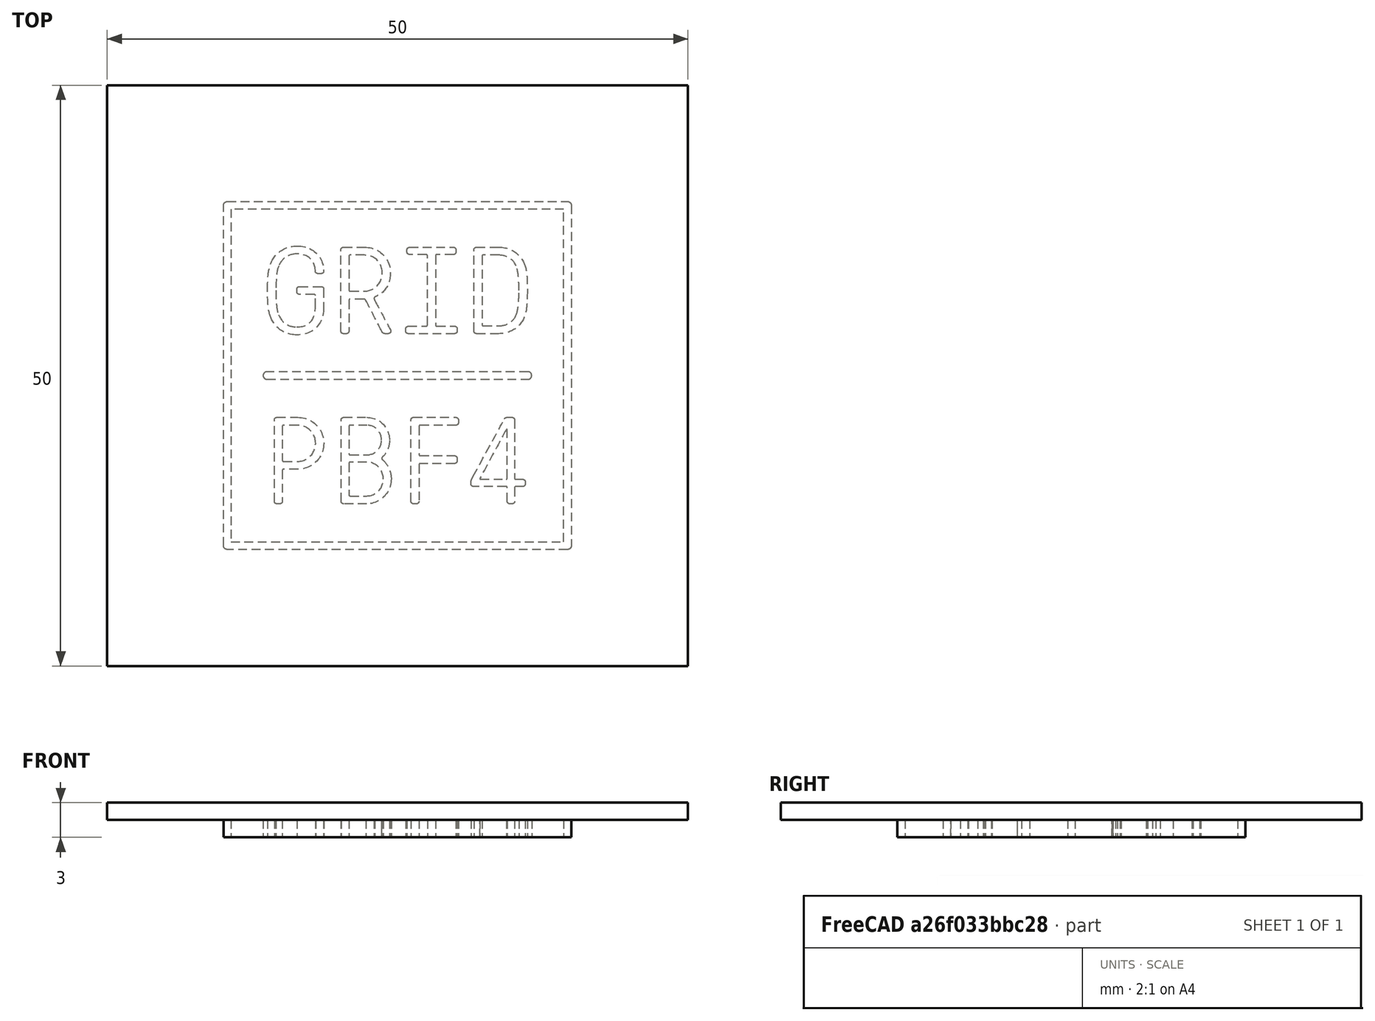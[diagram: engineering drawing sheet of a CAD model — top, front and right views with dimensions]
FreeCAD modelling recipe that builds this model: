
FCSTD DOCUMENT  (FreeCAD 0.18R16131 (Git))
Label: Pbf4 Logo 5cm
License: All rights reserved
LicenseURL: http://en.wikipedia.org/wiki/All_rights_reserved
objects: Sketcher::SketchObject×3, PartDesign::Pad×3, PartDesign::Body×1
note: 10 computed .brp shape members not serialized (recipe doc carries the construction recipe); baked Part::Feature solids carry a one-line shape summary decoded from their .brp

FEATURE [Sketcher::SketchObject] Sketch017
  sketch-geometry (12):
    g0: BSplineCurve PolesCount=2 KnotsCount=2 Degree=1 IsPeriodic=0
    g1: BSplineCurve PolesCount=2 KnotsCount=2 Degree=1 IsPeriodic=0
    g2: BSplineCurve PolesCount=2 KnotsCount=2 Degree=1 IsPeriodic=0
    g3: BSplineCurve PolesCount=2 KnotsCount=2 Degree=1 IsPeriodic=0
    g4: BSplineCurve PolesCount=2 KnotsCount=2 Degree=1 IsPeriodic=0
    g5: BSplineCurve PolesCount=4 KnotsCount=2 Degree=3 IsPeriodic=0
    g6: BSplineCurve PolesCount=2 KnotsCount=2 Degree=1 IsPeriodic=0
    g7: BSplineCurve PolesCount=4 KnotsCount=2 Degree=3 IsPeriodic=0
    g8: BSplineCurve PolesCount=2 KnotsCount=2 Degree=1 IsPeriodic=0
    g9: BSplineCurve PolesCount=4 KnotsCount=2 Degree=3 IsPeriodic=0
    g10: BSplineCurve PolesCount=2 KnotsCount=2 Degree=1 IsPeriodic=0
    g11: BSplineCurve PolesCount=4 KnotsCount=2 Degree=3 IsPeriodic=0
  constraints (12):
    c: Coincident(g0,g1)
    c: Coincident(g1,g2)
    c: Coincident(g2,g3)
    c: Coincident(g3,g0)
    c: Coincident(g4,g5)
    c: Coincident(g5,g6)
    c: Coincident(g6,g7)
    c: Coincident(g7,g8)
    c: Coincident(g8,g9)
    c: Coincident(g9,g10)
    c: Coincident(g10,g11)
    c: Coincident(g11,g4)
FEATURE [Sketcher::SketchObject] Sketch018
  sketch-geometry (189):
    g0: BSplineCurve PolesCount=4 KnotsCount=2 Degree=3 IsPeriodic=0
    g1: BSplineCurve PolesCount=4 KnotsCount=2 Degree=3 IsPeriodic=0
    g2: BSplineCurve PolesCount=4 KnotsCount=2 Degree=3 IsPeriodic=0
    g3: BSplineCurve PolesCount=2 KnotsCount=2 Degree=1 IsPeriodic=0
    g4: BSplineCurve PolesCount=4 KnotsCount=2 Degree=3 IsPeriodic=0
    g5: BSplineCurve PolesCount=2 KnotsCount=2 Degree=1 IsPeriodic=0
    g6: BSplineCurve PolesCount=4 KnotsCount=2 Degree=3 IsPeriodic=0
    g7: BSplineCurve PolesCount=2 KnotsCount=2 Degree=1 IsPeriodic=0
    g8: BSplineCurve PolesCount=4 KnotsCount=2 Degree=3 IsPeriodic=0
    g9: BSplineCurve PolesCount=2 KnotsCount=2 Degree=1 IsPeriodic=0
    g10: BSplineCurve PolesCount=4 KnotsCount=2 Degree=3 IsPeriodic=0
    g11: BSplineCurve PolesCount=2 KnotsCount=2 Degree=1 IsPeriodic=0
    g12: BSplineCurve PolesCount=4 KnotsCount=2 Degree=3 IsPeriodic=0
    g13: BSplineCurve PolesCount=2 KnotsCount=2 Degree=1 IsPeriodic=0
    g14: BSplineCurve PolesCount=4 KnotsCount=2 Degree=3 IsPeriodic=0
    g15: BSplineCurve PolesCount=2 KnotsCount=2 Degree=1 IsPeriodic=0
    g16: BSplineCurve PolesCount=4 KnotsCount=2 Degree=3 IsPeriodic=0
    g17: BSplineCurve PolesCount=2 KnotsCount=2 Degree=1 IsPeriodic=0
    g18: BSplineCurve PolesCount=4 KnotsCount=2 Degree=3 IsPeriodic=0
    g19: BSplineCurve PolesCount=2 KnotsCount=2 Degree=1 IsPeriodic=0
    g20: BSplineCurve PolesCount=4 KnotsCount=2 Degree=3 IsPeriodic=0
    g21: BSplineCurve PolesCount=2 KnotsCount=2 Degree=1 IsPeriodic=0
    g22: BSplineCurve PolesCount=4 KnotsCount=2 Degree=3 IsPeriodic=0
    g23: BSplineCurve PolesCount=2 KnotsCount=2 Degree=1 IsPeriodic=0
    g24: BSplineCurve PolesCount=4 KnotsCount=2 Degree=3 IsPeriodic=0
    g25: BSplineCurve PolesCount=2 KnotsCount=2 Degree=1 IsPeriodic=0
    g26: BSplineCurve PolesCount=4 KnotsCount=2 Degree=3 IsPeriodic=0
    g27: BSplineCurve PolesCount=2 KnotsCount=2 Degree=1 IsPeriodic=0
    g28: BSplineCurve PolesCount=4 KnotsCount=2 Degree=3 IsPeriodic=0
    g29: BSplineCurve PolesCount=4 KnotsCount=2 Degree=3 IsPeriodic=0
    g30: BSplineCurve PolesCount=2 KnotsCount=2 Degree=1 IsPeriodic=0
    g31: BSplineCurve PolesCount=4 KnotsCount=2 Degree=3 IsPeriodic=0
    g32: BSplineCurve PolesCount=2 KnotsCount=2 Degree=1 IsPeriodic=0
    g33: BSplineCurve PolesCount=4 KnotsCount=2 Degree=3 IsPeriodic=0
    g34: BSplineCurve PolesCount=2 KnotsCount=2 Degree=1 IsPeriodic=0
    g35: BSplineCurve PolesCount=4 KnotsCount=2 Degree=3 IsPeriodic=0
    g36: BSplineCurve PolesCount=4 KnotsCount=2 Degree=3 IsPeriodic=0
    g37: BSplineCurve PolesCount=2 KnotsCount=2 Degree=1 IsPeriodic=0
    g38: BSplineCurve PolesCount=4 KnotsCount=2 Degree=3 IsPeriodic=0
    g39: BSplineCurve PolesCount=2 KnotsCount=2 Degree=1 IsPeriodic=0
    g40: BSplineCurve PolesCount=4 KnotsCount=2 Degree=3 IsPeriodic=0
    g41: BSplineCurve PolesCount=2 KnotsCount=2 Degree=1 IsPeriodic=0
    g42: BSplineCurve PolesCount=4 KnotsCount=2 Degree=3 IsPeriodic=0
    g43: BSplineCurve PolesCount=2 KnotsCount=2 Degree=1 IsPeriodic=0
    g44: BSplineCurve PolesCount=4 KnotsCount=2 Degree=3 IsPeriodic=0
    g45: BSplineCurve PolesCount=2 KnotsCount=2 Degree=1 IsPeriodic=0
    g46: BSplineCurve PolesCount=4 KnotsCount=2 Degree=3 IsPeriodic=0
    g47: BSplineCurve PolesCount=4 KnotsCount=2 Degree=3 IsPeriodic=0
    g48: BSplineCurve PolesCount=4 KnotsCount=2 Degree=3 IsPeriodic=0
    g49: BSplineCurve PolesCount=4 KnotsCount=2 Degree=3 IsPeriodic=0
    g50: BSplineCurve PolesCount=4 KnotsCount=2 Degree=3 IsPeriodic=0
    g51: BSplineCurve PolesCount=2 KnotsCount=2 Degree=1 IsPeriodic=0
    g52: BSplineCurve PolesCount=4 KnotsCount=2 Degree=3 IsPeriodic=0
    g53: BSplineCurve PolesCount=4 KnotsCount=2 Degree=3 IsPeriodic=0
    g54: BSplineCurve PolesCount=2 KnotsCount=2 Degree=1 IsPeriodic=0
    g55: BSplineCurve PolesCount=4 KnotsCount=2 Degree=3 IsPeriodic=0
    g56: BSplineCurve PolesCount=2 KnotsCount=2 Degree=1 IsPeriodic=0
    g57: BSplineCurve PolesCount=4 KnotsCount=2 Degree=3 IsPeriodic=0
    g58: BSplineCurve PolesCount=2 KnotsCount=2 Degree=1 IsPeriodic=0
    g59: BSplineCurve PolesCount=4 KnotsCount=2 Degree=3 IsPeriodic=0
    g60: BSplineCurve PolesCount=2 KnotsCount=2 Degree=1 IsPeriodic=0
    g61: BSplineCurve PolesCount=4 KnotsCount=2 Degree=3 IsPeriodic=0
    g62: BSplineCurve PolesCount=2 KnotsCount=2 Degree=1 IsPeriodic=0
    g63: BSplineCurve PolesCount=4 KnotsCount=2 Degree=3 IsPeriodic=0
    g64: BSplineCurve PolesCount=4 KnotsCount=2 Degree=3 IsPeriodic=0
    g65: BSplineCurve PolesCount=2 KnotsCount=2 Degree=1 IsPeriodic=0
    g66: BSplineCurve PolesCount=4 KnotsCount=2 Degree=3 IsPeriodic=0
    g67: BSplineCurve PolesCount=2 KnotsCount=2 Degree=1 IsPeriodic=0
    g68: BSplineCurve PolesCount=4 KnotsCount=2 Degree=3 IsPeriodic=0
    g69: BSplineCurve PolesCount=2 KnotsCount=2 Degree=1 IsPeriodic=0
    g70: BSplineCurve PolesCount=4 KnotsCount=2 Degree=3 IsPeriodic=0
    g71: BSplineCurve PolesCount=2 KnotsCount=2 Degree=1 IsPeriodic=0
    g72: BSplineCurve PolesCount=4 KnotsCount=2 Degree=3 IsPeriodic=0
    g73: BSplineCurve PolesCount=2 KnotsCount=2 Degree=1 IsPeriodic=0
    g74: BSplineCurve PolesCount=4 KnotsCount=2 Degree=3 IsPeriodic=0
    g75: BSplineCurve PolesCount=2 KnotsCount=2 Degree=1 IsPeriodic=0
    g76: BSplineCurve PolesCount=4 KnotsCount=2 Degree=3 IsPeriodic=0
    g77: BSplineCurve PolesCount=2 KnotsCount=2 Degree=1 IsPeriodic=0
    g78: BSplineCurve PolesCount=4 KnotsCount=2 Degree=3 IsPeriodic=0
    g79: BSplineCurve PolesCount=2 KnotsCount=2 Degree=1 IsPeriodic=0
    g80: BSplineCurve PolesCount=4 KnotsCount=2 Degree=3 IsPeriodic=0
    g81: BSplineCurve PolesCount=2 KnotsCount=2 Degree=1 IsPeriodic=0
    g82: BSplineCurve PolesCount=4 KnotsCount=2 Degree=3 IsPeriodic=0
    g83: BSplineCurve PolesCount=2 KnotsCount=2 Degree=1 IsPeriodic=0
    g84: BSplineCurve PolesCount=4 KnotsCount=2 Degree=3 IsPeriodic=0
    g85: BSplineCurve PolesCount=2 KnotsCount=2 Degree=1 IsPeriodic=0
    g86: BSplineCurve PolesCount=4 KnotsCount=2 Degree=3 IsPeriodic=0
    g87: BSplineCurve PolesCount=2 KnotsCount=2 Degree=1 IsPeriodic=0
    g88: BSplineCurve PolesCount=4 KnotsCount=2 Degree=3 IsPeriodic=0
    g89: BSplineCurve PolesCount=2 KnotsCount=2 Degree=1 IsPeriodic=0
    g90: BSplineCurve PolesCount=4 KnotsCount=2 Degree=3 IsPeriodic=0
    g91: BSplineCurve PolesCount=2 KnotsCount=2 Degree=1 IsPeriodic=0
    g92: BSplineCurve PolesCount=4 KnotsCount=2 Degree=3 IsPeriodic=0
    g93: BSplineCurve PolesCount=2 KnotsCount=2 Degree=1 IsPeriodic=0
    g94: BSplineCurve PolesCount=4 KnotsCount=2 Degree=3 IsPeriodic=0
    g95: BSplineCurve PolesCount=2 KnotsCount=2 Degree=1 IsPeriodic=0
    g96: BSplineCurve PolesCount=4 KnotsCount=2 Degree=3 IsPeriodic=0
    g97: BSplineCurve PolesCount=2 KnotsCount=2 Degree=1 IsPeriodic=0
    g98: BSplineCurve PolesCount=4 KnotsCount=2 Degree=3 IsPeriodic=0
    g99: BSplineCurve PolesCount=4 KnotsCount=2 Degree=3 IsPeriodic=0
    g100: BSplineCurve PolesCount=2 KnotsCount=2 Degree=1 IsPeriodic=0
    g101: BSplineCurve PolesCount=4 KnotsCount=2 Degree=3 IsPeriodic=0
    g102: BSplineCurve PolesCount=4 KnotsCount=2 Degree=3 IsPeriodic=0
    g103: BSplineCurve PolesCount=2 KnotsCount=2 Degree=1 IsPeriodic=0
    g104: BSplineCurve PolesCount=4 KnotsCount=2 Degree=3 IsPeriodic=0
    g105: BSplineCurve PolesCount=4 KnotsCount=2 Degree=3 IsPeriodic=0
    g106: BSplineCurve PolesCount=4 KnotsCount=2 Degree=3 IsPeriodic=0
    g107: BSplineCurve PolesCount=4 KnotsCount=2 Degree=3 IsPeriodic=0
    g108: BSplineCurve PolesCount=4 KnotsCount=2 Degree=3 IsPeriodic=0
    g109: BSplineCurve PolesCount=4 KnotsCount=2 Degree=3 IsPeriodic=0
    g110: BSplineCurve PolesCount=2 KnotsCount=2 Degree=1 IsPeriodic=0
    g111: BSplineCurve PolesCount=4 KnotsCount=2 Degree=3 IsPeriodic=0
    g112: BSplineCurve PolesCount=4 KnotsCount=2 Degree=3 IsPeriodic=0
    g113: BSplineCurve PolesCount=4 KnotsCount=2 Degree=3 IsPeriodic=0
    g114: BSplineCurve PolesCount=4 KnotsCount=2 Degree=3 IsPeriodic=0
    g115: BSplineCurve PolesCount=4 KnotsCount=2 Degree=3 IsPeriodic=0
    g116: BSplineCurve PolesCount=4 KnotsCount=2 Degree=3 IsPeriodic=0
    g117: BSplineCurve PolesCount=4 KnotsCount=2 Degree=3 IsPeriodic=0
    g118: BSplineCurve PolesCount=2 KnotsCount=2 Degree=1 IsPeriodic=0
    g119: BSplineCurve PolesCount=4 KnotsCount=2 Degree=3 IsPeriodic=0
    g120: BSplineCurve PolesCount=2 KnotsCount=2 Degree=1 IsPeriodic=0
    g121: BSplineCurve PolesCount=4 KnotsCount=2 Degree=3 IsPeriodic=0
    g122: BSplineCurve PolesCount=2 KnotsCount=2 Degree=1 IsPeriodic=0
    g123: BSplineCurve PolesCount=4 KnotsCount=2 Degree=3 IsPeriodic=0
    g124: BSplineCurve PolesCount=2 KnotsCount=2 Degree=1 IsPeriodic=0
    g125: BSplineCurve PolesCount=4 KnotsCount=2 Degree=3 IsPeriodic=0
    g126: BSplineCurve PolesCount=2 KnotsCount=2 Degree=1 IsPeriodic=0
    g127: BSplineCurve PolesCount=4 KnotsCount=2 Degree=3 IsPeriodic=0
    g128: BSplineCurve PolesCount=4 KnotsCount=2 Degree=3 IsPeriodic=0
    g129: BSplineCurve PolesCount=2 KnotsCount=2 Degree=1 IsPeriodic=0
    g130: BSplineCurve PolesCount=4 KnotsCount=2 Degree=3 IsPeriodic=0
    g131: BSplineCurve PolesCount=2 KnotsCount=2 Degree=1 IsPeriodic=0
    g132: BSplineCurve PolesCount=4 KnotsCount=2 Degree=3 IsPeriodic=0
    g133: BSplineCurve PolesCount=4 KnotsCount=2 Degree=3 IsPeriodic=0
    g134: BSplineCurve PolesCount=4 KnotsCount=2 Degree=3 IsPeriodic=0
    g135: BSplineCurve PolesCount=4 KnotsCount=2 Degree=3 IsPeriodic=0
    g136: BSplineCurve PolesCount=2 KnotsCount=2 Degree=1 IsPeriodic=0
    g137: BSplineCurve PolesCount=4 KnotsCount=2 Degree=3 IsPeriodic=0
    g138: BSplineCurve PolesCount=4 KnotsCount=2 Degree=3 IsPeriodic=0
    g139: BSplineCurve PolesCount=2 KnotsCount=2 Degree=1 IsPeriodic=0
    g140: BSplineCurve PolesCount=4 KnotsCount=2 Degree=3 IsPeriodic=0
    g141: BSplineCurve PolesCount=2 KnotsCount=2 Degree=1 IsPeriodic=0
    g142: BSplineCurve PolesCount=4 KnotsCount=2 Degree=3 IsPeriodic=0
    g143: BSplineCurve PolesCount=2 KnotsCount=2 Degree=1 IsPeriodic=0
    g144: BSplineCurve PolesCount=4 KnotsCount=2 Degree=3 IsPeriodic=0
    g145: BSplineCurve PolesCount=2 KnotsCount=2 Degree=1 IsPeriodic=0
    g146: BSplineCurve PolesCount=4 KnotsCount=2 Degree=3 IsPeriodic=0
    g147: BSplineCurve PolesCount=2 KnotsCount=2 Degree=1 IsPeriodic=0
    g148: BSplineCurve PolesCount=4 KnotsCount=2 Degree=3 IsPeriodic=0
    g149: BSplineCurve PolesCount=4 KnotsCount=2 Degree=3 IsPeriodic=0
    g150: BSplineCurve PolesCount=2 KnotsCount=2 Degree=1 IsPeriodic=0
    g151: BSplineCurve PolesCount=4 KnotsCount=2 Degree=3 IsPeriodic=0
    g152: BSplineCurve PolesCount=2 KnotsCount=2 Degree=1 IsPeriodic=0
    g153: BSplineCurve PolesCount=4 KnotsCount=2 Degree=3 IsPeriodic=0
    g154: BSplineCurve PolesCount=2 KnotsCount=2 Degree=1 IsPeriodic=0
    g155: BSplineCurve PolesCount=4 KnotsCount=2 Degree=3 IsPeriodic=0
    g156: BSplineCurve PolesCount=2 KnotsCount=2 Degree=1 IsPeriodic=0
    g157: BSplineCurve PolesCount=4 KnotsCount=2 Degree=3 IsPeriodic=0
    g158: BSplineCurve PolesCount=2 KnotsCount=2 Degree=1 IsPeriodic=0
    g159: BSplineCurve PolesCount=4 KnotsCount=2 Degree=3 IsPeriodic=0
    g160: BSplineCurve PolesCount=2 KnotsCount=2 Degree=1 IsPeriodic=0
    g161: BSplineCurve PolesCount=4 KnotsCount=2 Degree=3 IsPeriodic=0
    g162: BSplineCurve PolesCount=2 KnotsCount=2 Degree=1 IsPeriodic=0
    g163: BSplineCurve PolesCount=4 KnotsCount=2 Degree=3 IsPeriodic=0
    g164: BSplineCurve PolesCount=2 KnotsCount=2 Degree=1 IsPeriodic=0
    g165: BSplineCurve PolesCount=4 KnotsCount=2 Degree=3 IsPeriodic=0
    g166: BSplineCurve PolesCount=2 KnotsCount=2 Degree=1 IsPeriodic=0
    g167: BSplineCurve PolesCount=4 KnotsCount=2 Degree=3 IsPeriodic=0
    g168: BSplineCurve PolesCount=2 KnotsCount=2 Degree=1 IsPeriodic=0
    g169: BSplineCurve PolesCount=4 KnotsCount=2 Degree=3 IsPeriodic=0
    g170: BSplineCurve PolesCount=2 KnotsCount=2 Degree=1 IsPeriodic=0
    g171: BSplineCurve PolesCount=4 KnotsCount=2 Degree=3 IsPeriodic=0
    g172: BSplineCurve PolesCount=2 KnotsCount=2 Degree=1 IsPeriodic=0
    g173: BSplineCurve PolesCount=4 KnotsCount=2 Degree=3 IsPeriodic=0
    g174: BSplineCurve PolesCount=2 KnotsCount=2 Degree=1 IsPeriodic=0
    g175: BSplineCurve PolesCount=4 KnotsCount=2 Degree=3 IsPeriodic=0
    g176: BSplineCurve PolesCount=2 KnotsCount=2 Degree=1 IsPeriodic=0
    g177: BSplineCurve PolesCount=4 KnotsCount=2 Degree=3 IsPeriodic=0
    g178: BSplineCurve PolesCount=2 KnotsCount=2 Degree=1 IsPeriodic=0
    g179: BSplineCurve PolesCount=4 KnotsCount=2 Degree=3 IsPeriodic=0
    g180: BSplineCurve PolesCount=2 KnotsCount=2 Degree=1 IsPeriodic=0
    g181: BSplineCurve PolesCount=4 KnotsCount=2 Degree=3 IsPeriodic=0
    g182: BSplineCurve PolesCount=2 KnotsCount=2 Degree=1 IsPeriodic=0
    g183: BSplineCurve PolesCount=4 KnotsCount=2 Degree=3 IsPeriodic=0
    g184: BSplineCurve PolesCount=4 KnotsCount=2 Degree=3 IsPeriodic=0
    g185: BSplineCurve PolesCount=4 KnotsCount=2 Degree=3 IsPeriodic=0
    g186: BSplineCurve PolesCount=4 KnotsCount=2 Degree=3 IsPeriodic=0
    g187: BSplineCurve PolesCount=2 KnotsCount=2 Degree=1 IsPeriodic=0
    g188: BSplineCurve PolesCount=4 KnotsCount=2 Degree=3 IsPeriodic=0
  constraints (189):
    c: Coincident(g0,g1)
    c: Coincident(g1,g2)
    c: Coincident(g2,g3)
    c: Coincident(g3,g4)
    c: Coincident(g4,g5)
    c: Coincident(g5,g6)
    c: Coincident(g6,g7)
    c: Coincident(g7,g8)
    c: Coincident(g8,g0)
    c: Coincident(g9,g10)
    c: Coincident(g10,g11)
    c: Coincident(g11,g12)
    c: Coincident(g12,g13)
    c: Coincident(g13,g14)
    c: Coincident(g14,g15)
    c: Coincident(g15,g16)
    c: Coincident(g16,g17)
    c: Coincident(g17,g18)
    c: Coincident(g18,g19)
    c: Coincident(g19,g20)
    c: Coincident(g20,g21)
    c: Coincident(g21,g22)
    c: Coincident(g22,g23)
    c: Coincident(g23,g24)
    c: Coincident(g24,g25)
    c: Coincident(g25,g26)
    c: Coincident(g26,g27)
    c: Coincident(g27,g28)
    c: Coincident(g28,g9)
    c: Coincident(g29,g30)
    c: Coincident(g30,g31)
    c: Coincident(g31,g32)
    c: Coincident(g32,g33)
    c: Coincident(g33,g34)
    c: Coincident(g34,g35)
    c: Coincident(g35,g29)
    c: Coincident(g36,g37)
    c: Coincident(g37,g38)
    c: Coincident(g38,g39)
    c: Coincident(g39,g40)
    c: Coincident(g40,g41)
    c: Coincident(g41,g42)
    c: Coincident(g42,g36)
    c: Coincident(g43,g44)
    c: Coincident(g44,g45)
    c: Coincident(g45,g46)
    c: Coincident(g46,g47)
    c: Coincident(g47,g48)
    c: Coincident(g48,g49)
    c: Coincident(g49,g50)
    c: Coincident(g50,g51)
    c: Coincident(g51,g52)
    c: Coincident(g52,g43)
    c: Coincident(g53,g54)
    c: Coincident(g54,g55)
    c: Coincident(g55,g56)
    c: Coincident(g56,g57)
    c: Coincident(g57,g58)
    c: Coincident(g58,g59)
    c: Coincident(g59,g53)
    c: Coincident(g60,g61)
    c: Coincident(g61,g62)
    c: Coincident(g62,g63)
    c: Coincident(g63,g64)
    c: Coincident(g64,g65)
    c: Coincident(g65,g66)
    c: Coincident(g66,g67)
    c: Coincident(g67,g68)
    c: Coincident(g68,g69)
    c: Coincident(g69,g70)
    c: Coincident(g70,g60)
    c: Coincident(g71,g72)
    c: Coincident(g72,g73)
    c: Coincident(g73,g74)
    c: Coincident(g74,g75)
    c: Coincident(g75,g76)
    c: Coincident(g76,g77)
    c: Coincident(g77,g78)
    c: Coincident(g78,g79)
    c: Coincident(g79,g80)
    c: Coincident(g80,g81)
    c: Coincident(g81,g82)
    c: Coincident(g82,g83)
    c: Coincident(g83,g84)
    c: Coincident(g84,g85)
    c: Coincident(g85,g86)
    c: Coincident(g86,g87)
    c: Coincident(g87,g88)
    c: Coincident(g88,g89)
    c: Coincident(g89,g90)
    c: Coincident(g90,g91)
    c: Coincident(g91,g92)
    c: Coincident(g92,g71)
    c: Coincident(g93,g94)
    c: Coincident(g94,g95)
    c: Coincident(g95,g96)
    c: Coincident(g96,g97)
    c: Coincident(g97,g98)
    c: Coincident(g98,g93)
    c: Coincident(g99,g100)
    c: Coincident(g100,g101)
    c: Coincident(g101,g102)
    c: Coincident(g102,g103)
    c: Coincident(g103,g104)
    c: Coincident(g104,g99)
    c: Coincident(g105,g106)
    c: Coincident(g106,g107)
    c: Coincident(g107,g108)
    c: Coincident(g108,g109)
    c: Coincident(g109,g110)
    c: Coincident(g110,g111)
    c: Coincident(g111,g112)
    c: Coincident(g112,g113)
    c: Coincident(g113,g114)
    c: Coincident(g114,g115)
    c: Coincident(g115,g116)
    c: Coincident(g116,g117)
    c: Coincident(g117,g118)
    c: Coincident(g118,g119)
    c: Coincident(g119,g120)
    c: Coincident(g120,g121)
    c: Coincident(g121,g122)
    c: Coincident(g122,g123)
    c: Coincident(g123,g124)
    c: Coincident(g124,g125)
    c: Coincident(g125,g126)
    c: Coincident(g126,g127)
    c: Coincident(g127,g128)
    c: Coincident(g128,g105)
    c: Coincident(g129,g130)
    c: Coincident(g130,g131)
    c: Coincident(g131,g132)
    c: Coincident(g132,g133)
    c: Coincident(g133,g134)
    c: Coincident(g134,g135)
    c: Coincident(g135,g136)
    c: Coincident(g136,g137)
    c: Coincident(g137,g138)
    c: Coincident(g138,g139)
    c: Coincident(g139,g140)
    c: Coincident(g140,g141)
    c: Coincident(g141,g142)
    c: Coincident(g142,g143)
    c: Coincident(g143,g144)
    c: Coincident(g144,g145)
    c: Coincident(g145,g146)
    c: Coincident(g146,g147)
    c: Coincident(g147,g148)
    c: Coincident(g148,g129)
    c: Coincident(g149,g150)
    c: Coincident(g150,g151)
    c: Coincident(g151,g152)
    c: Coincident(g152,g153)
    c: Coincident(g153,g154)
    c: Coincident(g154,g155)
    c: Coincident(g155,g149)
    c: Coincident(g156,g157)
    c: Coincident(g157,g158)
    c: Coincident(g158,g159)
    c: Coincident(g159,g160)
    c: Coincident(g160,g161)
    c: Coincident(g161,g162)
    c: Coincident(g162,g163)
    c: Coincident(g163,g164)
    c: Coincident(g164,g165)
    c: Coincident(g165,g166)
    c: Coincident(g166,g167)
    c: Coincident(g167,g168)
    c: Coincident(g168,g169)
    c: Coincident(g169,g170)
    c: Coincident(g170,g171)
    c: Coincident(g171,g172)
    c: Coincident(g172,g173)
    c: Coincident(g173,g174)
    c: Coincident(g174,g175)
    c: Coincident(g175,g176)
    c: Coincident(g176,g177)
    c: Coincident(g177,g178)
    c: Coincident(g178,g179)
    c: Coincident(g179,g156)
    c: Coincident(g180,g181)
    c: Coincident(g181,g182)
    c: Coincident(g182,g183)
    c: Coincident(g183,g184)
    c: Coincident(g184,g185)
    c: Coincident(g185,g186)
    c: Coincident(g186,g187)
    c: Coincident(g187,g188)
    c: Coincident(g188,g180)
FEATURE [Sketcher::SketchObject] Sketch
  MapMode = 5
  Support = -> [XY_Plane]
  sketch-geometry (5):
    g0: LineSegment StartX=-25 StartY=25 StartZ=0 EndX=-25 EndY=-25 EndZ=0
    g1: LineSegment StartX=-25 StartY=-25 StartZ=0 EndX=25 EndY=-25 EndZ=0
    g2: LineSegment StartX=25 StartY=-25 StartZ=0 EndX=25 EndY=25 EndZ=0
    g3: LineSegment StartX=25 StartY=25 StartZ=0 EndX=-25 EndY=25 EndZ=0
    g4: Circle [constr] CenterX=0 CenterY=0 CenterZ=0 NormalX=0 NormalY=0 NormalZ=1 AngleXU=0 Radius=35.3553
  constraints (14):
    c: Coincident(g0,g1)
    c: Coincident(g1,g2)
    c: Coincident(g2,g3)
    c: Coincident(g3,g0)
    c: Equal(g0,g1)
    c: Equal(g0,g2)
    c: Equal(g0,g3)
    c: PointOnObject(g0,g4)
    c: PointOnObject(g1,g4)
    c: PointOnObject(g2,g4)
    c: PointOnObject(g3,g4)
    c: Coincident(g4,g-1)
    c: Horizontal(g3)
    c: DistanceX(g3,g3) = 50
FEATURE [PartDesign::Pad] Pad
  Length = 1.5
  Length2 = 100
  Profile = -> Sketch
  Type = 0
FEATURE [PartDesign::Pad] Pad001
  BaseFeature = -> Pad
  Length = 1.5
  Length2 = 100
  Profile = -> Sketch017
  Reversed = true
  Type = 0
FEATURE [PartDesign::Pad] Pad002
  BaseFeature = -> Pad001
  Length = 1.5
  Length2 = 100
  Profile = -> Sketch018
  Reversed = true
  Type = 0
FEATURE [PartDesign::Body] Body
  Group = -> [Sketch,Pad,Sketch017,Sketch018,Pad001,Pad002]
  Origin = -> Origin
  Tip = -> Pad002
